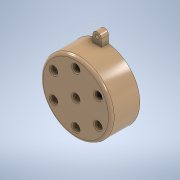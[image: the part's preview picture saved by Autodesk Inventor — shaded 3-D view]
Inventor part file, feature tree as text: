
AUTODESK INVENTOR PART (.ipt)
format: ipt  version: 2021 (Build 250183000, 183)  size: 190,976 bytes
history: native  units: mm
features: sketch x10, extrude x3, other x1, fillet x1, chamfer x1, pattern_circular x1, mirror x1
ambient origin geometry x8: Origin, YZ Plane, XZ Plane, XY Plane, X Axis, Y Axis, Z Axis, Center Point
bodies: Body1 (feature_tree)
feature tree (18):
  other  "Sólido1"
  extrude  "Extrusão1"  Depth=20.0mm TaperAngle=0.0deg
  fillet  "Arredondamento1"  Radius=2.0mm
  extrude  "Extrusão2"  Depth=5.0mm
  chamfer  "Chanfro1"  Distance=15.0mm
  pattern_circular  "Padrão circular1"  Count=6 Angle=360.0deg
  extrude  "Extrusão3"  Depth=3.0mm
  mirror  "Espelhamento1"
  sketch  "Esboço4"  dims[d9=0.6mm d10=2.0mm d11=45.0deg d12=60.0mm d13=360.0deg]
  sketch  "Esboço5"  dims[d15=6.0mm d16=3.0mm]
  sketch  "Esboço6"  dims[d17=30.0mm]
  sketch  "Esboço7"  dims[d18=5.0mm d19=0.0mm]
  sketch  "Esboço8"
  sketch  "Esboço9"
  sketch  "Esboço10"
  sketch  "Esboço1"  dims[d0=50.0mm d1=20.0mm d2=0.0mm d3=2.0mm]
  sketch  "Esboço2"  dims[d4=5.0mm d5=5.0mm]
  sketch  "Esboço3"  dims[d6=18.0mm d7=15.0mm d8=0.0mm]
